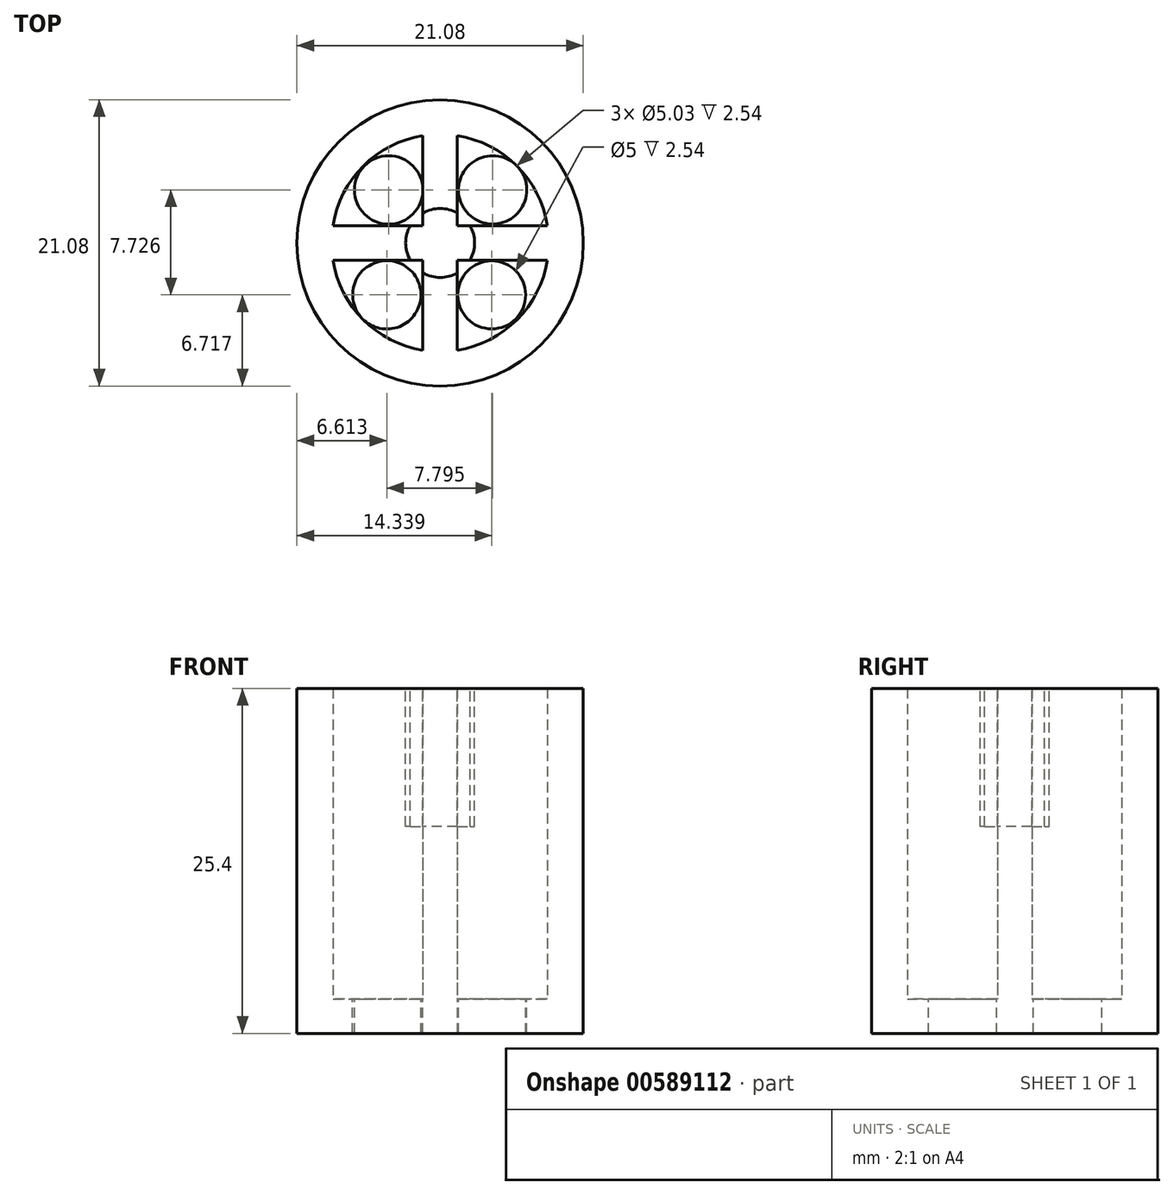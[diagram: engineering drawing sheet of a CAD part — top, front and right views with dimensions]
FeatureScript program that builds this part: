
annotation { "Feature Type Name" : "Feature", "Feature Type Description" : "" }
export const myFeature = defineFeature(function(context is Context, id is Id, definition is map)
    precondition{}
    {
        {
            var Q0;
            Q0=qCreatedBy(makeId("Top.planeOp"),FACE);
            var sketch = newSketch(context, id + "F0", { "sketchPlane" : qUnion([Q0])});
            skCircle(sketch, "E0", {"center": v(0, 0) * mm, "radius": 10.54 * mm});
            skSolve(sketch);
        }
        {
            var Q0;
            Q0=qSketchRegion(id+"F0",true);
            extrude(context, id + "F1", {"entities" : qUnion([Q0]), "depth" : 25.4 * mm, "offsetDistance" : 25.4 * mm});
        }
        {
            var Q0;
            Q0=makeQuery(id+"F1.opExtrude","CAP_FACE",FACE,{"disambiguationData":[OSD([sQuery(id+"F0.wireOp",EDGE,"E0")])],"isStart":false});
            var sketch = newSketch(context, id + "F2", { "sketchPlane" : qUnion([Q0])});
            skCircle(sketch, "E1", {"center": v(0, 0) * mm, "radius": 8 * mm});
            skSolve(sketch);
        }
        {
            var Q0;
            Q0=qSketchRegion(id+"F2",true);
            extrude(context, id + "F3", {"entities" : qUnion([Q0]), "operationType" : NewBodyOperationType.REMOVE, "oppositeDirection" : true, "depth" : 22.86 * mm, "offsetDistance" : 25.4 * mm});
        }
        {
            var Q0;
            Q0=makeQuery(id+"F3.boolean.opBoolean","COPY",FACE,{"derivedFrom":makeQuery(id+"F3.opExtrude","CAP_FACE",FACE,{"disambiguationData":[OSD([sQuery(id+"F2.wireOp",EDGE,"E1")])],"isStart":false})});
            var sketch = newSketch(context, id + "F4", { "sketchPlane" : qUnion([Q0])});
            skLineSegment(sketch, "E2", {"start": v(-1.27, -7.9) * mm, "end": v(-1.27, 7.9) * mm});
            skLineSegment(sketch, "E3", {"start": v(1.27, -7.9) * mm, "end": v(1.27, 7.9) * mm});
            skLineSegment(sketch, "E4", {"start": v(-7.9, 1.27) * mm, "end": v(7.9, 1.27) * mm});
            skLineSegment(sketch, "E5", {"start": v(-7.9, -1.27) * mm, "end": v(7.9, -1.27) * mm});
            skSolve(sketch);
        }
        {
            var Q0;
            Q0=qSketchRegion(id+"F4",true);
            var Q1;
            {var subQ0=sQuery(id+"F4.wireOp",EDGE,"E5");var subQ1=sQuery(id+"F4.wireOp",EDGE,"E3");var subQ2=makeQuery(id+"F4.imprint","INTERSECT",VERTEX,{"derivedFrom":[subQ1,subQ0]});Q1=makeQuery(id+"F4.imprint","IMPRINT",FACE,{"disambiguationData":[TD([[makeQuery(id+"F4.imprint","IMPRINT",EDGE,{"disambiguationData":[TD([[subQ2,-1.0]])],"derivedFrom":subQ1}),-1.0]])]});}
            var Q2;
            {var subQ0=sQuery(id+"F4.wireOp",EDGE,"E2");var subQ1=makeQuery(id+"F3.boolean.opBoolean","COPY",EDGE,{"derivedFrom":makeQuery(id+"F3.opExtrude","CAP_EDGE",EDGE,{"disambiguationData":[OSD([sQuery(id+"F2.wireOp",EDGE,"E1")])],"isStart":false})});var subQ2=makeQuery(id+"F4.imprint","INTERSECT",VERTEX,{"disambiguationData":[OD(1.0)],"derivedFrom":[subQ1,subQ0]});Q2=makeQuery(id+"F4.imprint","IMPRINT",FACE,{"disambiguationData":[TD([[makeQuery(id+"F4.imprint","IMPRINT",EDGE,{"disambiguationData":[TD([[subQ2,1.0]])],"derivedFrom":subQ0}),-1.0]])]});}
            var Q3;
            {var subQ0=sQuery(id+"F4.wireOp",EDGE,"E5");var subQ1=sQuery(id+"F4.wireOp",EDGE,"E2");var subQ2=makeQuery(id+"F4.imprint","INTERSECT",VERTEX,{"derivedFrom":[subQ1,subQ0]});Q3=makeQuery(id+"F4.imprint","IMPRINT",FACE,{"disambiguationData":[TD([[makeQuery(id+"F4.imprint","IMPRINT",EDGE,{"disambiguationData":[TD([[subQ2,-1.0]])],"derivedFrom":subQ1}),1.0]])]});}
            var Q4;
            {var subQ0=sQuery(id+"F4.wireOp",EDGE,"E2");var subQ1=makeQuery(id+"F3.boolean.opBoolean","COPY",EDGE,{"derivedFrom":makeQuery(id+"F3.opExtrude","CAP_EDGE",EDGE,{"disambiguationData":[OSD([sQuery(id+"F2.wireOp",EDGE,"E1")])],"isStart":false})});var subQ2=makeQuery(id+"F4.imprint","INTERSECT",VERTEX,{"disambiguationData":[OD(0.0)],"derivedFrom":[subQ1,subQ0]});Q4=makeQuery(id+"F4.imprint","IMPRINT",FACE,{"disambiguationData":[TD([[makeQuery(id+"F4.imprint","IMPRINT",EDGE,{"disambiguationData":[TD([[subQ2,-1.0]])],"derivedFrom":subQ0}),-1.0]])]});}
            extrude(context, id + "F5", {"entities" : qUnion([Q0, Q1, Q2, Q3, Q4]), "operationType" : NewBodyOperationType.ADD, "depth" : 22.86 * mm, "offsetDistance" : 25.4 * mm});
        }
        {
            var Q0;
            Q0=makeQuery(id+"F5.boolean.opBoolean","MERGE",FACE,{"derivedFrom":[makeQuery(id+"F1.opExtrude","CAP_FACE",FACE,{"disambiguationData":[OSD([sQuery(id+"F0.wireOp",EDGE,"E0")])],"isStart":false}),makeQuery(id+"F5.opExtrude","CAP_FACE",FACE,{"disambiguationData":[OSD([sQuery(id+"F2.wireOp",EDGE,"E1"),sQuery(id+"F4.wireOp",EDGE,"E2"),sQuery(id+"F4.wireOp",EDGE,"E3"),sQuery(id+"F4.wireOp",EDGE,"E4"),sQuery(id+"F4.wireOp",EDGE,"E5")])],"isStart":false})]});
            var sketch = newSketch(context, id + "F6", { "sketchPlane" : qUnion([Q0])});
            skCircle(sketch, "E6", {"center": v(0, 0) * mm, "radius": 2.54 * mm});
            skSolve(sketch);
        }
        {
            var Q0;
            Q0 = qSketchRegion(id + "F6", true);
            extrude(context, id + "F7", {"entities" : qUnion([Q0]), "operationType" : NewBodyOperationType.REMOVE, "oppositeDirection" : true, "depth" : 10.16 * mm, "offsetDistance" : 25.4 * mm});
        }
        {
            var Q0;
            {var subQ0=sQuery(id+"F2.wireOp",EDGE,"E1");var subQ1=sQuery(id+"F4.wireOp",EDGE,"E2");var subQ2=makeQuery(id+"F3.boolean.opBoolean","COPY",EDGE,{"derivedFrom":makeQuery(id+"F3.opExtrude","CAP_EDGE",EDGE,{"disambiguationData":[OSD([subQ0])],"isStart":false})});Q0=makeQuery(id+"F5.boolean.opBoolean","SPLIT",FACE,{"disambiguationData":[TD([makeQuery(id+"F5.opExtrude","SWEPT_FACE",FACE,{"disambiguationData":[OSD([subQ1]),TDD([makeQuery(id+"F4.imprint","IMPRINT",EDGE,{"disambiguationData":[TD([[makeQuery(id+"F4.imprint","INTERSECT",VERTEX,{"disambiguationData":[OD(0.0)],"derivedFrom":[subQ2,subQ1]}),-1.0]])],"derivedFrom":subQ1})])]})])],"derivedFrom":makeQuery(id+"F3.boolean.opBoolean","COPY",FACE,{"derivedFrom":makeQuery(id+"F3.opExtrude","CAP_FACE",FACE,{"disambiguationData":[OSD([subQ0])],"isStart":false})})});}
            var sketch = newSketch(context, id + "F8", { "sketchPlane" : qUnion([Q0])});
            skCircle(sketch, "E7", {"center": v(-3.93, -3.82) * mm, "radius": 2.51 * mm});
            skCircle(sketch, "E8", {"center": v(-3.79, 3.9) * mm, "radius": 2.51 * mm});
            skCircle(sketch, "E9", {"center": v(3.87, 3.9) * mm, "radius": 2.51 * mm});
            skCircle(sketch, "E10", {"center": v(3.8, -3.82) * mm, "radius": 2.5 * mm});
            skSolve(sketch);
        }
        {
            var Q0;
            Q0=makeQuery(id+"F8.imprint","IMPRINT",FACE,{"disambiguationData":[TD([[makeQuery(id+"F8.imprint","IMPRINT",EDGE,{"derivedFrom":sQuery(id+"F8.wireOp",EDGE,"E8")}),1.0]])]});
            var Q1;
            Q1=makeQuery(id+"F8.imprint","IMPRINT",FACE,{"disambiguationData":[TD([[makeQuery(id+"F8.imprint","IMPRINT",EDGE,{"derivedFrom":sQuery(id+"F8.wireOp",EDGE,"E9")}),1.0]])]});
            var Q2;
            Q2=makeQuery(id+"F8.imprint","IMPRINT",FACE,{"disambiguationData":[TD([[makeQuery(id+"F8.imprint","IMPRINT",EDGE,{"derivedFrom":sQuery(id+"F8.wireOp",EDGE,"E10")}),1.0]])]});
            var Q3;
            Q3=makeQuery(id+"F8.imprint","IMPRINT",FACE,{"disambiguationData":[TD([[makeQuery(id+"F8.imprint","IMPRINT",EDGE,{"derivedFrom":sQuery(id+"F8.wireOp",EDGE,"E7")}),1.0]])]});
            extrude(context, id + "F9", {"entities" : qUnion([Q0, Q1, Q2, Q3]), "operationType" : NewBodyOperationType.REMOVE, "endBound" : BoundingType.THROUGH_ALL, "oppositeDirection" : true, "depth" : 25.4 * mm, "offsetDistance" : 25.4 * mm});
        }
    });
